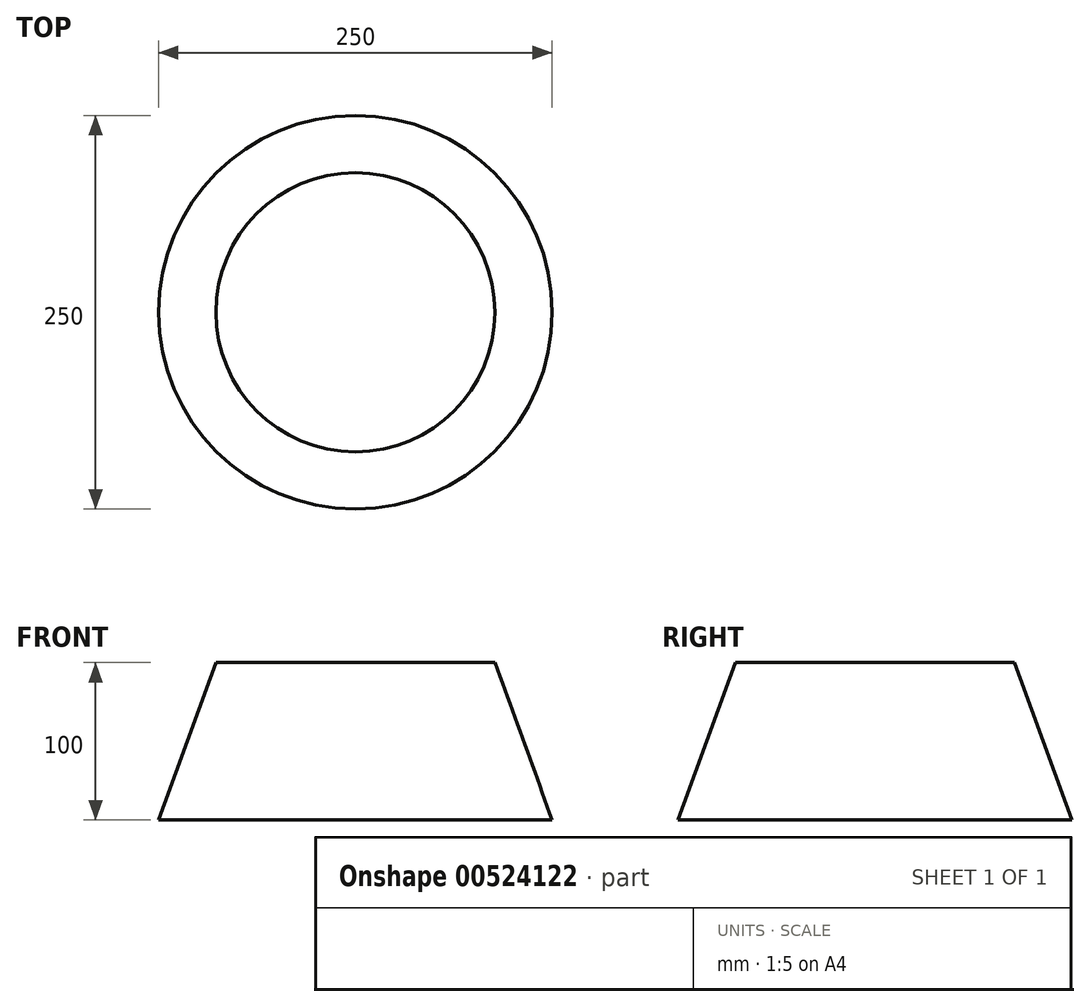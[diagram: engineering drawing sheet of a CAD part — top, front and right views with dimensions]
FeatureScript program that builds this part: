
annotation { "Feature Type Name" : "Feature", "Feature Type Description" : "" }
export const myFeature = defineFeature(function(context is Context, id is Id, definition is map)
    precondition{}
    {
        {
            var Q0;
            Q0=qCreatedBy(makeId("Top.planeOp"),FACE);
            var sketch = newSketch(context, id + "F0", { "sketchPlane" : qUnion([Q0])});
            skCircle(sketch, "E0", {"center": v(0, 0) * mm, "radius": 125 * mm});
            skSolve(sketch);
        }
        {
            var Q0;
            Q0 = qSketchRegion(id + "F0", true);
            extrude(context, id + "F1", {"entities" : qUnion([Q0]), "depth" : 100 * mm, "offsetDistance" : 25 * mm});
        }
        {
            var Q0;
            Q0=makeQuery(id+"F1.opExtrude","CAP_EDGE",EDGE,{"disambiguationData":[OSD([sQuery(id+"F0.wireOp",EDGE,"E0")])],"isStart":false});
            chamfer(context, id + "F2", {"entities" : qUnion([Q0]), "chamferType" : ChamferType.OFFSET_ANGLE, "width" : 100 * mm, "oppositeDirection" : true, "angle" : 20 * degree, "tangentPropagation" : true});
        }
    });
